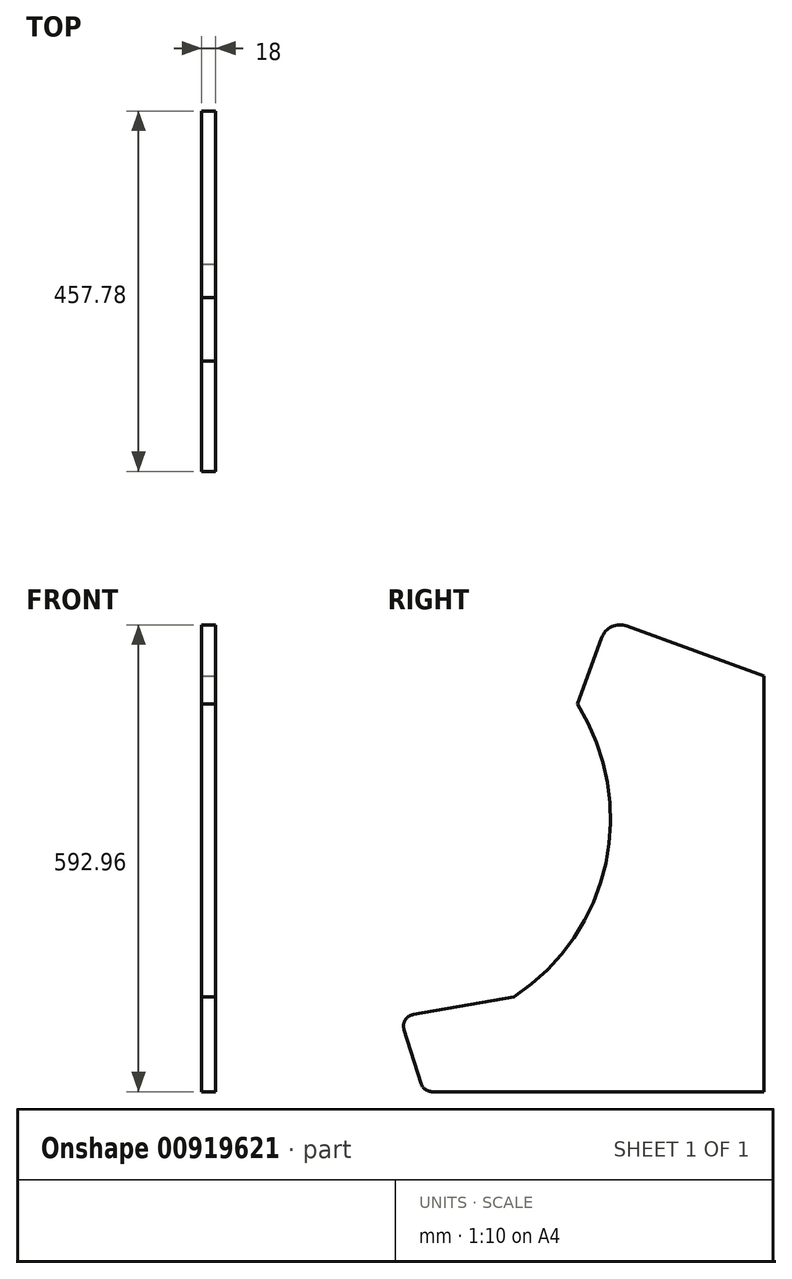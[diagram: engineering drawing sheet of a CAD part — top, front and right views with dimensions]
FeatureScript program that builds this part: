
annotation { "Feature Type Name" : "Feature", "Feature Type Description" : "" }
export const myFeature = defineFeature(function(context is Context, id is Id, definition is map)
    precondition{}
    {
        {
            var Q0;
            Q0=qCreatedBy(makeId("Right.planeOp"),FACE);
            var sketch = newSketch(context, id + "F0", { "sketchPlane" : qUnion([Q0])});
            skLineSegment(sketch, "E0", {"start": v(20.16, 27.2) * mm, "end": v(0.4, 34.39) * mm});
            skLineSegment(sketch, "E1", {"start": v(0.4, 34.39) * mm, "end": v(-3.52, 23.62) * mm});
            skLineSegment(sketch, "E2", {"start": v(20.16, 27.2) * mm, "end": v(20.16, -25.61) * mm});
            skLineSegment(sketch, "E3", {"start": v(20.16, -25.61) * mm, "end": v(-23.07, -25.61) * mm});
            skLineSegment(sketch, "E4", {"start": v(-23.07, -25.61) * mm, "end": v(-26.07, -16.11) * mm});
            skLineSegment(sketch, "E5", {"start": v(-26.07, -16.11) * mm, "end": v(-11.6, -13.56) * mm});
            skPoint(sketch, "E6.second.point", {"position": v(-51.42, 6.17) * mm});
            skPoint(sketch, "E6.third.point", {"position": v(-37.65, -9.55) * mm});
            skArc(sketch, "E7", {"start": v(-11.6, -13.56) * mm, "mid": v(0.07, 3.37) * mm, "end": v(-3.52, 23.62) * mm});
            skLineSegment(sketch, "E8", {"start": v(-55.33, -16.11) * mm, "end": v(41.51, -16.11) * mm, "construction": true});
            skLineSegment(sketch, "E9", {"start": v(-11.88, 27.2) * mm, "end": v(42.18, 27.2) * mm, "construction": true});
            skLineSegment(sketch, "E10", {"start": v(20.16, 27.2) * mm, "end": v(20.16, -40.98) * mm, "construction": true});
            skLineSegment(sketch, "E11", {"start": v(20.16, -30.61) * mm, "end": v(-34.84, -30.61) * mm, "construction": true});
            skSolve(sketch);
        }
        {
            var Q0;
            Q0=qSketchRegion(id+"F0",true);
            extrude(context, id + "F1", {"entities" : qUnion([Q0]), "oppositeDirection" : true, "depth" : 1.8 * mm});
        }
        {
            var Q0;
            Q0=makeQuery(id+"F1.opExtrude","SWEPT_EDGE",EDGE,{"disambiguationData":[OSD([sQuery(id+"F0.wireOp",EDGE,"E4"),sQuery(id+"F0.wireOp",EDGE,"E5")])]});
            var Q1;
            Q1=makeQuery(id+"F1.opExtrude","SWEPT_EDGE",EDGE,{"disambiguationData":[OSD([sQuery(id+"F0.wireOp",EDGE,"E3"),sQuery(id+"F0.wireOp",EDGE,"E4")])]});
            fillet(context, id + "F2", {"entities" : qUnion([Q0, Q1]), "radius" : 1.5 * mm, "tangentPropagation" : true, "allowEdgeOverflow" : false});
        }
        {
            var Q0;
            Q0=makeQuery(id+"F1.opExtrude","SWEPT_EDGE",EDGE,{"disambiguationData":[OSD([sQuery(id+"F0.wireOp",EDGE,"E0"),sQuery(id+"F0.wireOp",EDGE,"E1")])]});
            fillet(context, id + "F3", {"entities" : qUnion([Q0]), "radius" : 2.5 * mm, "tangentPropagation" : true, "allowEdgeOverflow" : false});
        }
        {
            var Q0;
            Q0=makeQuery(id+"F1.opExtrude","SWEPT_BODY",BODY,{"disambiguationData":[OSD([sQuery(id+"F0.wireOp",EDGE,"E0"),sQuery(id+"F0.wireOp",EDGE,"E1"),sQuery(id+"F0.wireOp",EDGE,"E2"),sQuery(id+"F0.wireOp",EDGE,"E3"),sQuery(id+"F0.wireOp",EDGE,"E4"),sQuery(id+"F0.wireOp",EDGE,"E5"),sQuery(id+"F0.wireOp",EDGE,"E7")])]});
            var Q1;
            Q1=makeQuery(id+"F1.opExtrude","CAP_VERTEX",VERTEX,{"disambiguationData":[OSD([sQuery(id+"F0.wireOp",EDGE,"E2"),sQuery(id+"F0.wireOp",EDGE,"E3")])],"isStart":true});
            transform(context, id + "F4", {"entities" : qUnion([Q0]), "transformType" : TransformType.SCALE_UNIFORMLY, "scale" : 10, "makeCopy" : false, "scalePoint" : qUnion([Q1])});
        }
    });
